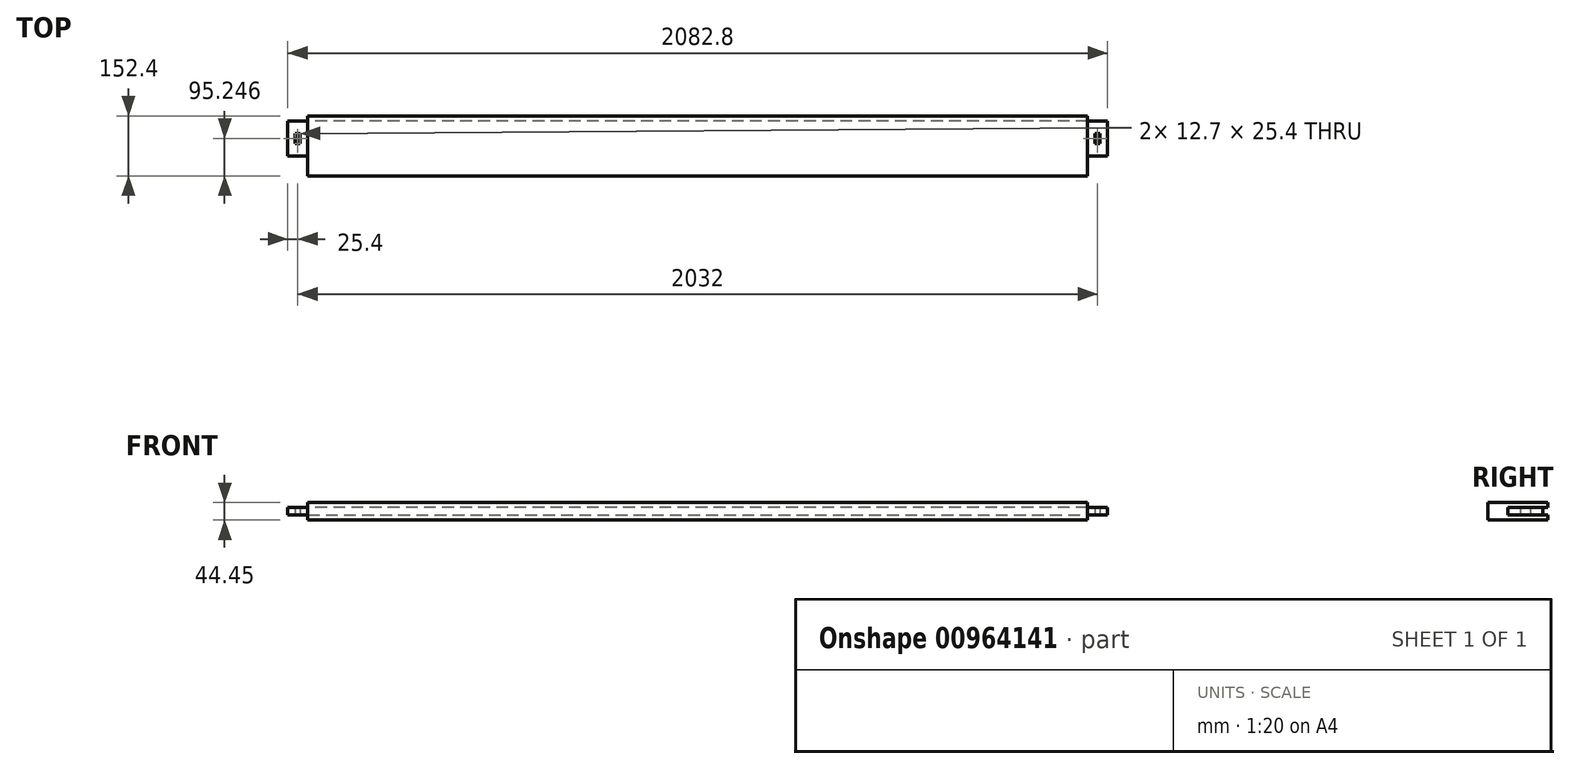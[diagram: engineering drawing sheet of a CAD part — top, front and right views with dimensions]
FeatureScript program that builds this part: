
annotation { "Feature Type Name" : "Feature", "Feature Type Description" : "" }
export const myFeature = defineFeature(function(context is Context, id is Id, definition is map)
    precondition{}
    {
        {
            var Q0;
            Q0=qCreatedBy(makeId("Top.planeOp"),FACE);
            var sketch = newSketch(context, id + "F0", { "sketchPlane" : qUnion([Q0])});
            skLineSegment(sketch, "E0.bottom", {"start": v(-960.45, -440.41) * mm, "end": v(1020.75, -440.41) * mm});
            skLineSegment(sketch, "E0.top", {"start": v(-960.45, -592.81) * mm, "end": v(1020.75, -592.81) * mm});
            skLineSegment(sketch, "E0.left", {"start": v(-960.45, -440.41) * mm, "end": v(-960.45, -592.81) * mm});
            skLineSegment(sketch, "E0.right", {"start": v(1020.75, -440.41) * mm, "end": v(1020.75, -592.81) * mm});
            skLineSegment(sketch, "E1.bottom", {"start": v(-960.45, -542.01) * mm, "end": v(-1011.25, -542.01) * mm});
            skLineSegment(sketch, "E1.top", {"start": v(-960.45, -440.41) * mm, "end": v(-1011.25, -440.41) * mm});
            skLineSegment(sketch, "E1.left", {"start": v(-960.45, -542.01) * mm, "end": v(-960.45, -440.41) * mm});
            skLineSegment(sketch, "E1.right", {"start": v(-1011.25, -542.01) * mm, "end": v(-1011.25, -440.41) * mm});
            skLineSegment(sketch, "E2.bottom", {"start": v(1020.75, -440.41) * mm, "end": v(1071.55, -440.41) * mm});
            skLineSegment(sketch, "E2.top", {"start": v(1020.75, -542.01) * mm, "end": v(1071.55, -542.01) * mm});
            skLineSegment(sketch, "E2.left", {"start": v(1020.75, -440.41) * mm, "end": v(1020.75, -542.01) * mm});
            skLineSegment(sketch, "E2.right", {"start": v(1071.55, -440.41) * mm, "end": v(1071.55, -542.01) * mm});
            skSolve(sketch);
        }
        {
            var Q0;
            Q0 = qSketchRegion(id + "F0", true);
            extrude(context, id + "F1", {"entities" : qUnion([Q0]), "depth" : 44.45 * mm, "offsetDistance" : 25.4 * mm});
        }
        {
            var Q0;
            Q0=qCreatedBy(makeId("Top.planeOp"),FACE);
            var sketch = newSketch(context, id + "F2", { "sketchPlane" : qUnion([Q0])});
            skLineSegment(sketch, "E3.bottom", {"start": v(-1011.25, -440.41) * mm, "end": v(-960.45, -440.41) * mm});
            skLineSegment(sketch, "E3.top", {"start": v(-1011.25, -542.01) * mm, "end": v(-960.45, -542.01) * mm});
            skLineSegment(sketch, "E3.left", {"start": v(-1011.25, -440.41) * mm, "end": v(-1011.25, -542.01) * mm});
            skLineSegment(sketch, "E3.right", {"start": v(-960.45, -440.41) * mm, "end": v(-960.45, -542.01) * mm});
            skLineSegment(sketch, "E4.bottom", {"start": v(1020.75, -440.41) * mm, "end": v(1071.55, -440.41) * mm});
            skLineSegment(sketch, "E4.top", {"start": v(1020.75, -542.01) * mm, "end": v(1071.55, -542.01) * mm});
            skLineSegment(sketch, "E4.left", {"start": v(1020.75, -440.41) * mm, "end": v(1020.75, -542.01) * mm});
            skLineSegment(sketch, "E4.right", {"start": v(1071.55, -440.41) * mm, "end": v(1071.55, -542.01) * mm});
            skSolve(sketch);
        }
        {
            var Q0;
            Q0 = qSketchRegion(id + "F2", true);
            extrude(context, id + "F3", {"entities" : qUnion([Q0]), "operationType" : NewBodyOperationType.REMOVE, "depth" : 12.7 * mm, "offsetDistance" : 25.4 * mm});
        }
        {
            var Q0;
            Q0=makeQuery(id+"F1.opExtrude","CAP_FACE",FACE,{"disambiguationData":[OSD([sQuery(id+"F0.wireOp",EDGE,"E0.bottom"),sQuery(id+"F0.wireOp",EDGE,"E0.top"),sQuery(id+"F0.wireOp",EDGE,"E0.left"),sQuery(id+"F0.wireOp",EDGE,"E0.right"),sQuery(id+"F0.wireOp",EDGE,"E1.bottom"),sQuery(id+"F0.wireOp",EDGE,"E1.top"),sQuery(id+"F0.wireOp",EDGE,"E1.right"),sQuery(id+"F0.wireOp",EDGE,"E2.bottom"),sQuery(id+"F0.wireOp",EDGE,"E2.top"),sQuery(id+"F0.wireOp",EDGE,"E2.right")])],"isStart":false});
            var sketch = newSketch(context, id + "F4", { "sketchPlane" : qUnion([Q0])});
            skLineSegment(sketch, "E5.bottom", {"start": v(1020.75, -542.01) * mm, "end": v(1071.55, -542.01) * mm});
            skLineSegment(sketch, "E5.top", {"start": v(1020.75, -440.41) * mm, "end": v(1071.55, -440.41) * mm});
            skLineSegment(sketch, "E5.left", {"start": v(1020.75, -542.01) * mm, "end": v(1020.75, -440.41) * mm});
            skLineSegment(sketch, "E5.right", {"start": v(1071.55, -542.01) * mm, "end": v(1071.55, -440.41) * mm});
            skLineSegment(sketch, "E6.bottom", {"start": v(-960.45, -542.01) * mm, "end": v(-1011.25, -542.01) * mm});
            skLineSegment(sketch, "E6.top", {"start": v(-960.45, -440.41) * mm, "end": v(-1011.25, -440.41) * mm});
            skLineSegment(sketch, "E6.left", {"start": v(-960.45, -542.01) * mm, "end": v(-960.45, -440.41) * mm});
            skLineSegment(sketch, "E6.right", {"start": v(-1011.25, -542.01) * mm, "end": v(-1011.25, -440.41) * mm});
            skSolve(sketch);
        }
        {
            var Q0;
            Q0 = qSketchRegion(id + "F4", true);
            extrude(context, id + "F5", {"entities" : qUnion([Q0]), "operationType" : NewBodyOperationType.REMOVE, "oppositeDirection" : true, "depth" : 12.7 * mm, "offsetDistance" : 25.4 * mm});
        }
        {
            var Q0;
            Q0=makeQuery(id+"F1.opExtrude","SWEPT_FACE",FACE,{"disambiguationData":[OSD([sQuery(id+"F0.wireOp",EDGE,"E0.bottom"),sQuery(id+"F0.wireOp",EDGE,"E1.top"),sQuery(id+"F0.wireOp",EDGE,"E2.bottom")])]});
            var sketch = newSketch(context, id + "F6", { "sketchPlane" : qUnion([Q0])});
            skLineSegment(sketch, "E7.bottom", {"start": v(-1071.55, 31.75) * mm, "end": v(1011.25, 31.75) * mm});
            skLineSegment(sketch, "E7.top", {"start": v(-1071.55, 12.7) * mm, "end": v(1011.25, 12.7) * mm});
            skLineSegment(sketch, "E7.left", {"start": v(-1071.55, 31.75) * mm, "end": v(-1071.55, 12.7) * mm});
            skLineSegment(sketch, "E7.right", {"start": v(1011.25, 31.75) * mm, "end": v(1011.25, 12.7) * mm});
            skSolve(sketch);
        }
        {
            var Q0;
            Q0 = qSketchRegion(id + "F6", true);
            extrude(context, id + "F7", {"entities" : qUnion([Q0]), "operationType" : NewBodyOperationType.REMOVE, "oppositeDirection" : true, "depth" : 12.7 * mm, "offsetDistance" : 25.4 * mm});
        }
        {
            var Q0;
            Q0=makeQuery(id+"F3.boolean.opBoolean","COPY",FACE,{"derivedFrom":makeQuery(id+"F3.opExtrude","CAP_FACE",FACE,{"disambiguationData":[OSD([sQuery(id+"F2.wireOp",EDGE,"E3.bottom"),sQuery(id+"F2.wireOp",EDGE,"E3.top"),sQuery(id+"F2.wireOp",EDGE,"E3.left"),sQuery(id+"F2.wireOp",EDGE,"E3.right")])],"isStart":false})});
            var sketch = newSketch(context, id + "F8", { "sketchPlane" : qUnion([Q0])});
            skLineSegment(sketch, "E8.bottom", {"start": v(-992.2, 484.86) * mm, "end": v(-979.5, 484.86) * mm});
            skLineSegment(sketch, "E8.top", {"start": v(-992.2, 510.26) * mm, "end": v(-979.5, 510.26) * mm});
            skLineSegment(sketch, "E8.left", {"start": v(-992.2, 484.86) * mm, "end": v(-992.2, 510.26) * mm});
            skLineSegment(sketch, "E8.right", {"start": v(-979.5, 484.86) * mm, "end": v(-979.5, 510.26) * mm});
            skLineSegment(sketch, "E9.bottom", {"start": v(1039.8, 484.86) * mm, "end": v(1052.5, 484.86) * mm});
            skLineSegment(sketch, "E9.top", {"start": v(1039.8, 510.26) * mm, "end": v(1052.5, 510.26) * mm});
            skLineSegment(sketch, "E9.left", {"start": v(1039.8, 484.86) * mm, "end": v(1039.8, 510.26) * mm});
            skLineSegment(sketch, "E9.right", {"start": v(1052.5, 484.86) * mm, "end": v(1052.5, 510.26) * mm});
            skSolve(sketch);
        }
        {
            var Q0;
            Q0 = qSketchRegion(id + "F8", true);
            extrude(context, id + "F9", {"entities" : qUnion([Q0]), "operationType" : NewBodyOperationType.REMOVE, "endBound" : BoundingType.THROUGH_ALL, "oppositeDirection" : true, "depth" : 25.4 * mm, "offsetDistance" : 25.4 * mm});
        }
    });
